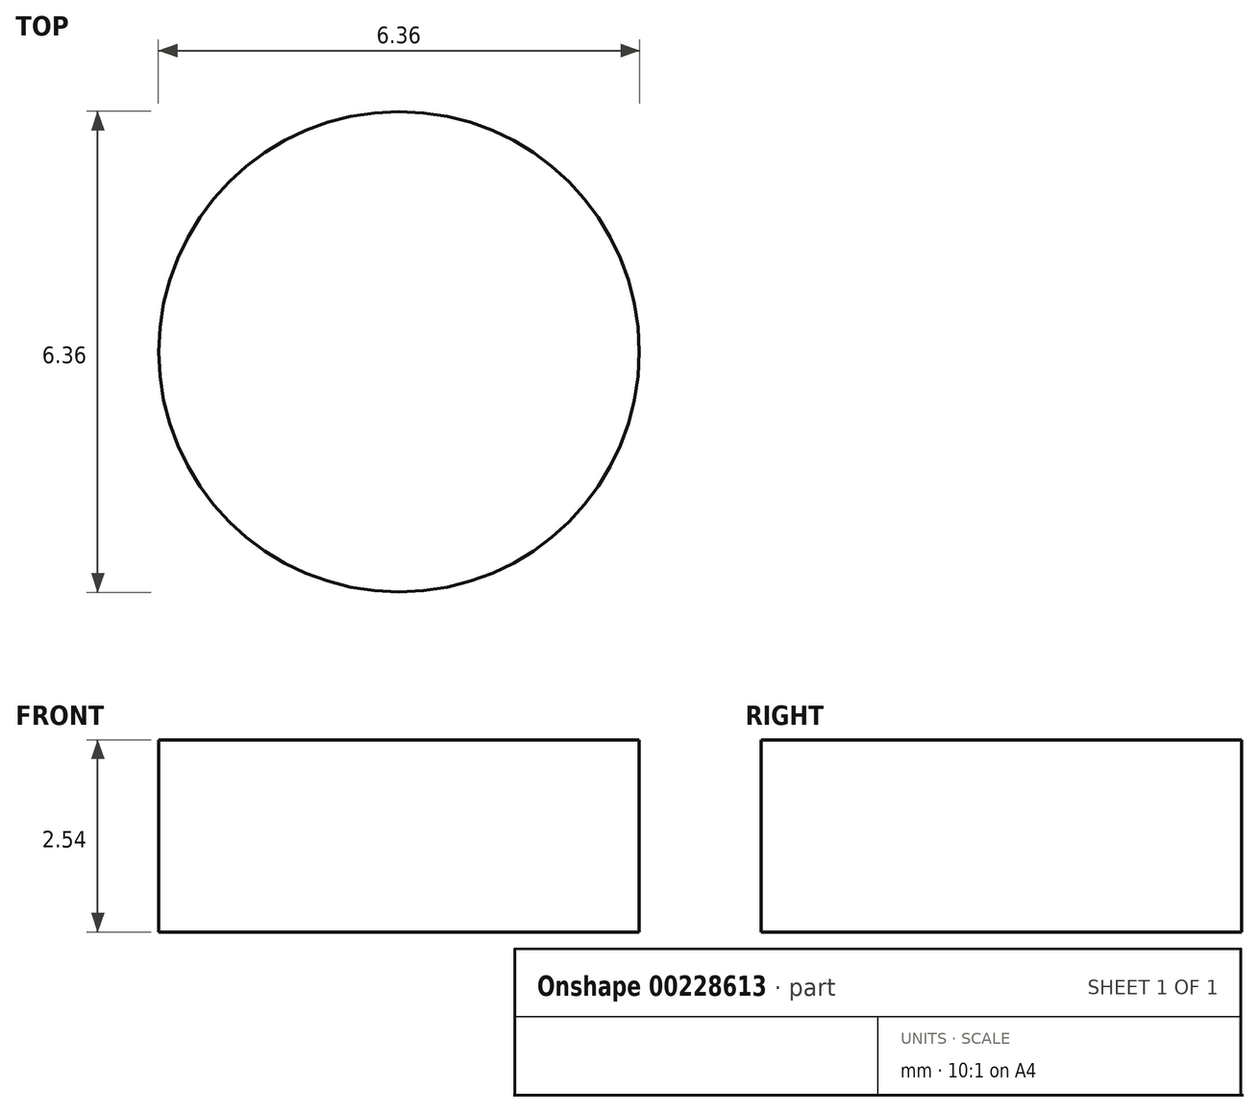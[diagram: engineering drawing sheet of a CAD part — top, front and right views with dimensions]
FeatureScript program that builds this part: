
annotation { "Feature Type Name" : "Feature", "Feature Type Description" : "" }
export const myFeature = defineFeature(function(context is Context, id is Id, definition is map)
    precondition{}
    {
        {
            var Q0;
            Q0=qCreatedBy(makeId("Top.planeOp"),FACE);
            var sketch = newSketch(context, id + "F0", { "sketchPlane" : qUnion([Q0])});
            skCircle(sketch, "E0", {"center": v(0, 0) * mm, "radius": 3.18 * mm});
            skSolve(sketch);
        }
        {
            var Q0;
            Q0 = qSketchRegion(id + "F0", true);
            extrude(context, id + "F1", {"entities" : qUnion([Q0]), "endBound" : BoundingType.SYMMETRIC, "depth" : 2.54 * mm});
        }
    });
